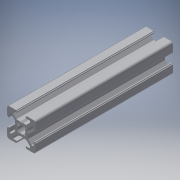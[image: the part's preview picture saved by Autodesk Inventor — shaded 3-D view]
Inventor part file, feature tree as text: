
AUTODESK INVENTOR PART (.ipt)
format: ipt  version: 2019 (Build 230136000, 136)  size: 311,296 bytes
history: native  units: in
note: dims shown in document units (in); Inventor stores cm internally (conversion verified against a paired STEP export)
features: other x3, extrude x1, sketch x1
ambient origin geometry x8: Origin, YZ Plane, XZ Plane, XY Plane, X Axis, Y Axis, Z Axis, Center Point
bodies: Solid1 (feature_tree)
feature tree (5):
  other  "Blocks"
  extrude  "Extrusion1"  Depth=1.0in
  sketch  "Sketch1"  dims[d1=0.0in d13=1.0in d14=1.0in]
  other  "20x20"
  other  "20x20:1"
